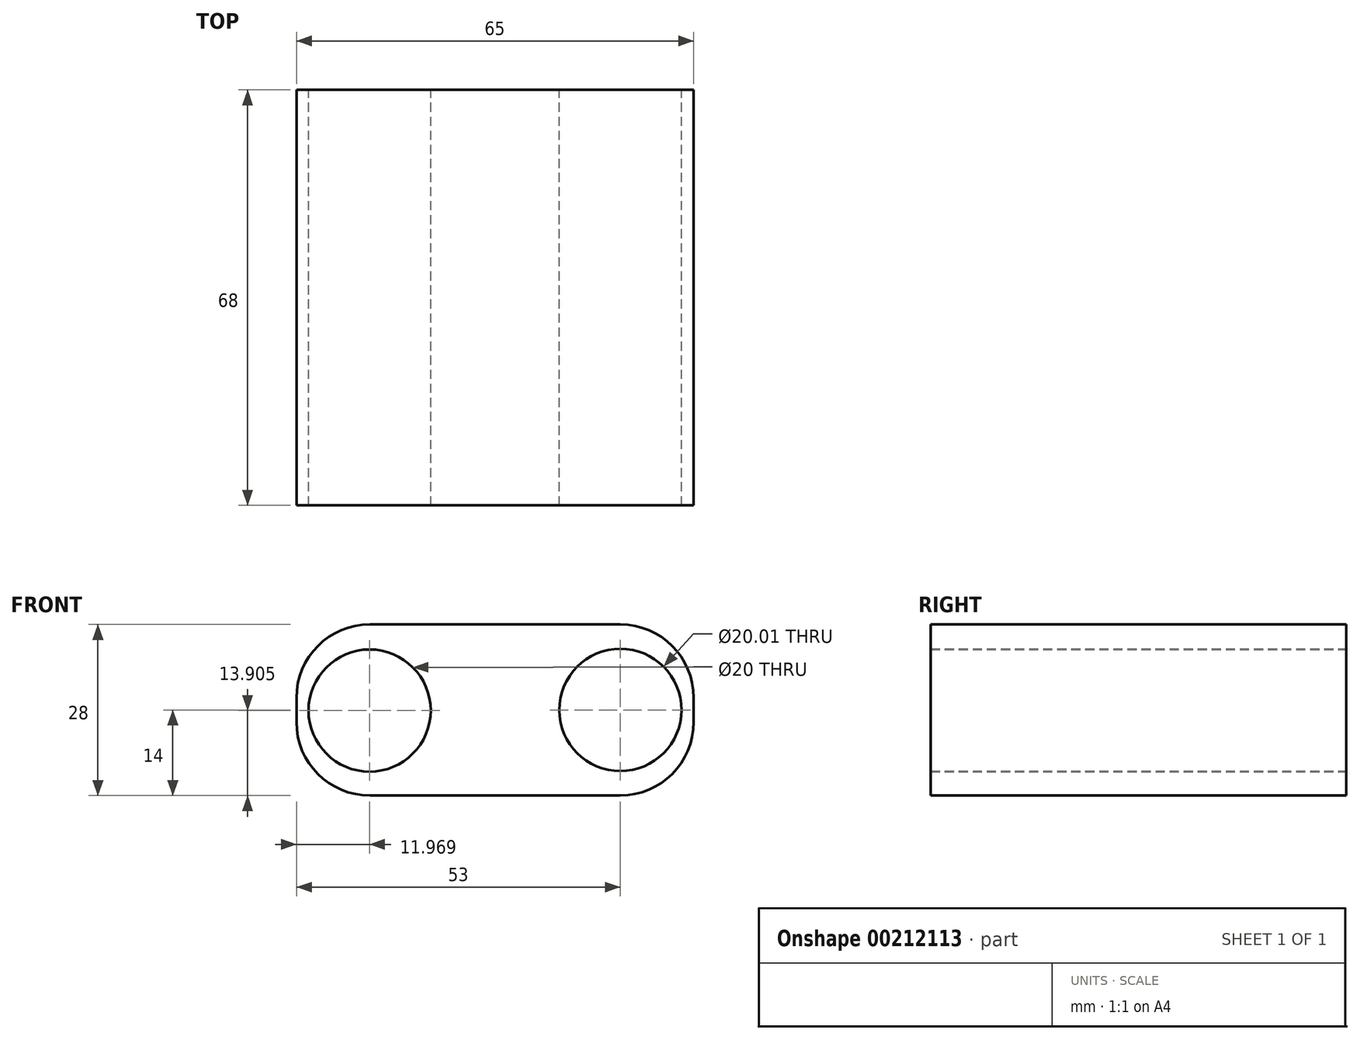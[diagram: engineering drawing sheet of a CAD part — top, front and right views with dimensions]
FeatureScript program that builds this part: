
annotation { "Feature Type Name" : "Feature", "Feature Type Description" : "" }
export const myFeature = defineFeature(function(context is Context, id is Id, definition is map)
    precondition{}
    {
        {
            var Q0;
            Q0=qCreatedBy(makeId("Front.planeOp"),FACE);
            var sketch = newSketch(context, id + "F0", { "sketchPlane" : qUnion([Q0])});
            skLineSegment(sketch, "E0.bottom", {"start": v(12, 0) * mm, "end": v(53, 0) * mm});
            skLineSegment(sketch, "E0.top", {"start": v(12, 28) * mm, "end": v(53, 28) * mm});
            skLineSegment(sketch, "E0.left", {"start": v(0, 12) * mm, "end": v(0, 16) * mm});
            skLineSegment(sketch, "E0.right", {"start": v(65, 12) * mm, "end": v(65, 16) * mm});
            skPoint(sketch, "E1.visualSharp", {"position": v(65, 28) * mm});
            skArc(sketch, "E1.filletArc", {"start": v(65, 16) * mm, "mid": v(61.49, 24.49) * mm, "end": v(53, 28) * mm});
            skPoint(sketch, "E2.visualSharp", {"position": v(65, 0) * mm});
            skArc(sketch, "E2.filletArc", {"start": v(53, 0) * mm, "mid": v(61.49, 3.51) * mm, "end": v(65, 12) * mm});
            skPoint(sketch, "E3.visualSharp", {"position": v(0, 0) * mm});
            skArc(sketch, "E3.filletArc", {"start": v(0, 12) * mm, "mid": v(3.51, 3.51) * mm, "end": v(12, 0) * mm});
            skPoint(sketch, "E4.visualSharp", {"position": v(0, 28) * mm});
            skArc(sketch, "E4.filletArc", {"start": v(12, 28) * mm, "mid": v(3.51, 24.49) * mm, "end": v(0, 16) * mm});
            skCircle(sketch, "E5", {"center": v(53, 14) * mm, "radius": 10 * mm});
            skCircle(sketch, "E6", {"center": v(11.97, 13.9) * mm, "radius": 10 * mm});
            skSolve(sketch);
        }
        {
            var Q0;
            Q0 = qSketchRegion(id + "F0", true);
            extrude(context, id + "F1", {"entities" : qUnion([Q0]), "depth" : 68 * mm});
        }
    });
